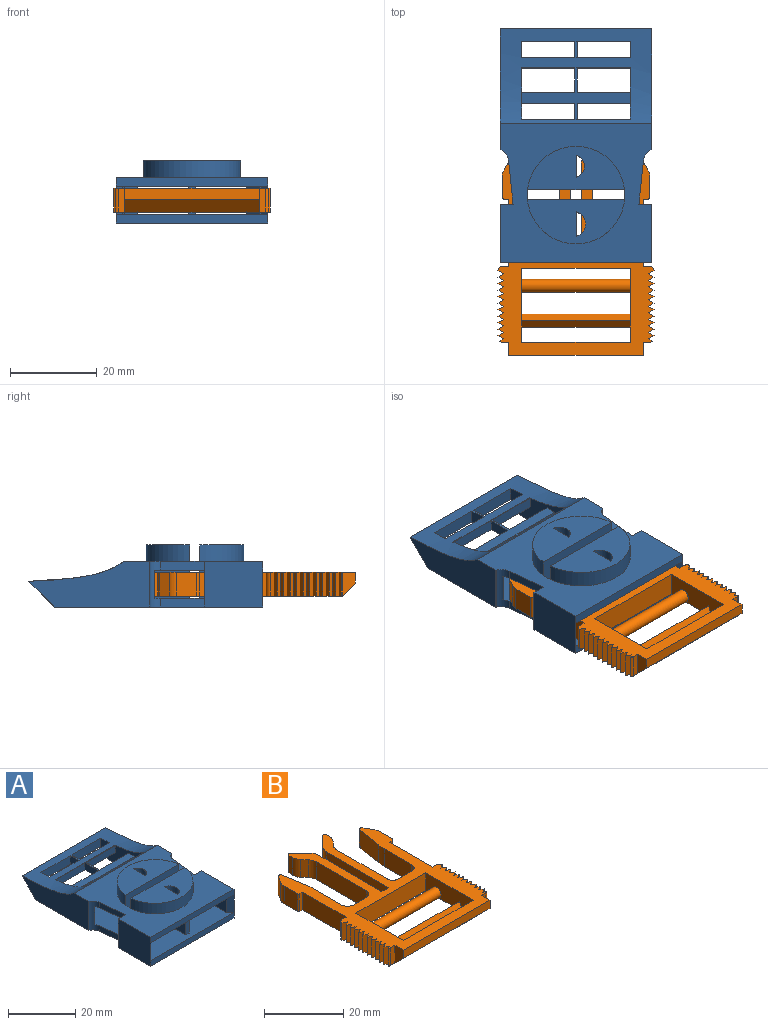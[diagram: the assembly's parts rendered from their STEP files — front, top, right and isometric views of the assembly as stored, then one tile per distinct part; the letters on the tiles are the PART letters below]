
ASSEMBLY  parts=2 mates=1
PART A: 76 faces, bbox 35x54x14.3 mm
  f0: cylinder r=11.25mm len=22.4mm, axis (0,0,-1), area 126.4mm2, adj f9,f29,f71
  f1: plane 48x35mm, normal (0,0,-1), area 1181.1mm2, adj f23,f24,f26,f27,f28,f32,f33,f34
  f2: plane 35x33mm, normal (0,0,1), area 912.1mm2, adj f4,f5,f6,f7,f23,f24,f25,f30
  f3: plane 35x33mm, normal (0,0,-1), area 912.1mm2, adj f4,f5,f6,f7,f23,f25,f30,f31
  f4: plane 16.2x6.5mm, normal (-1,0,0), area 105.3mm2, adj f2,f3,f23,f70
  f5: plane 8.53x6.5mm, normal (1,0,0), area 55.5mm2, adj f2,f3,f23,f69
  f6: plane 6.5x3.1mm, normal (1,0,0), area 20.2mm2, adj f2,f3,f67,f71
  f7: plane 6.5x3.15mm, normal (1,0,0), area 20.5mm2, adj f2,f3,f69,f70
  f8: plane 22.36x10.03mm, normal (0,0,1), area 163.8mm2, adj f65,f68,f69,f70
  f9: plane 22.4x10.22mm, normal (0,0,1), area 166.2mm2, adj f0,f66,f67,f71
  f10: plane 3.75x0.5mm, normal (0,0.06,1), area 1.9mm2, adj f12,f13,f44
  f11: plane 3.75x1mm, normal (0,-0.26,-0.97), area 1.9mm2, adj f12,f13,f17,f45
  f12: plane 3.75x3.3mm, normal (1,0,0), area 10.1mm2, adj f10,f11,f15,f35
  f13: plane 3.75x3.3mm, normal (-1,0,0), area 10.1mm2, adj f10,f11,f14,f36
  f14: plane 12.25x3.07mm, normal (0,-1,0), area 37.6mm2, adj f13,f33,f44,f45
  f15: plane 12.25x2.3mm, normal (0,1,0), area 28.1mm2, adj f12,f17,f32,f44
  f16: plane 25x11.93mm, normal (0,0,1), area 71.7mm2, adj f18,f19,f20,f21,f22,f23,f32,f33
  f17: plane 25x14.25mm, normal (0,0,-1), area 129.6mm2, adj f11,f15,f18,f19,f20,f21,f22,f23
  f18: plane 5.5x2.5mm, normal (1,0,0), area 13.7mm2, adj f16,f17,f20,f21
  f19: plane 5.5x2.5mm, normal (-1,0,0), area 13.7mm2, adj f16,f17,f41,f42
  f20: plane 12.25x2.5mm, normal (0,-1,0), area 30.6mm2, adj f16,f17,f18,f32
  f21: plane 12.25x2.5mm, normal (0,1,0), area 30.6mm2, adj f16,f17,f18,f32
  f22: plane 12.25x2.5mm, normal (0,-1,0), area 30.6mm2, adj f16,f17,f32,f63
  f23: plane 25x9.83mm, normal (0,1,0), area 91mm2, adj f1,f2,f3,f4,f5,f16,f17,f32
  f24: plane 35x2mm, normal (0,-1,0), area 70mm2, adj f1,f2,f27,f28
  f25: plane 6.5x0.4mm, normal (0,-1,0), area 2.6mm2, adj f2,f3,f38,f60
  f26: plane 27.93x10.5mm, normal (1,0,0), area 202mm2, adj f1,f29,f44,f45,f51
  f27: plane 13.5x10.5mm, normal (1,0,0), area 141.8mm2, adj f1,f24,f29,f37,f55,f61
  f28: plane 13.5x10.5mm, normal (-1,0,0), area 141.8mm2, adj f1,f24,f29,f37,f49,f62
  f29: plane 35x32.08mm, normal (0,0,1), area 668.9mm2, adj f0,f26,f27,f28,f34,f37,f44,f47
  f30: plane 12x6.5mm, normal (-1,0,0), area 78mm2, adj f2,f3,f55,f61
  f31: plane 6.5x3.15mm, normal (1,0,0), area 20.5mm2, adj f2,f3,f40,f48
  f32: plane 19.91x10.02mm, normal (-1,0,0), area 125.2mm2, adj f1,f2,f3,f15,f16,f17,f20,f21
  f33: plane 19.91x10.02mm, normal (1,0,0), area 125.2mm2, adj f1,f2,f3,f14,f16,f17,f23,f36
  f34: plane 27.93x10.5mm, normal (-1,0,0), area 202mm2, adj f1,f29,f44,f45,f50
  f35: plane 12.25x3.07mm, normal (0,-1,0), area 37.6mm2, adj f12,f32,f44,f45
  f36: plane 12.25x2.3mm, normal (0,1,0), area 28.1mm2, adj f13,f17,f33,f44
  f37: plane 35x2mm, normal (0,-1,0), area 70mm2, adj f3,f27,f28,f29
  f38: plane 6.5x3.15mm, normal (-1,0,0), area 20.5mm2, adj f2,f3,f25,f52
  f39: plane 12x6.5mm, normal (1,0,0), area 78mm2, adj f2,f3,f49,f62
  f40: plane 6.5x0.4mm, normal (0,-1,0), area 2.6mm2, adj f2,f3,f31,f59
  f41: plane 12.25x2.5mm, normal (0,-1,0), area 30.6mm2, adj f16,f17,f19,f33
  f42: plane 12.25x2.5mm, normal (0,1,0), area 30.6mm2, adj f16,f17,f19,f33
  f43: plane 12.25x2.5mm, normal (0,-1,0), area 30.6mm2, adj f16,f17,f33,f64
  f44: extruded ~35x21.85mm, area 386.4mm2, adj f10,f14,f15,f16,f23,f26,f29,f32
  f45: plane 35x5.92mm, normal (0,0.71,-0.71), area 187.2mm2, adj f1,f11,f14,f26,f32,f33,f34,f35
  f46: plane 10.07x2mm, normal (-0.99,-0.1,0), area 20.2mm2, adj f1,f2,f48,f49
  f47: plane 10.07x2mm, normal (-0.99,-0.1,0), area 20.2mm2, adj f3,f29,f48,f49
  f48: cylinder r=3mm len=10.5mm, axis (0,0,1), area 24.6mm2, adj f1,f2,f3,f29,f31,f46,f47,f50
  f49: plane 10.5x3mm, normal (0,1,0), area 21.8mm2, adj f1,f2,f3,f28,f29,f39,f46,f47
  f50: plane 10.5x0.14mm, normal (-0.39,-0.92,0), area 1.6mm2, adj f1,f29,f34,f48
  f51: plane 10.5x0.14mm, normal (0.39,-0.92,0), area 1.6mm2, adj f1,f26,f29,f52
  f52: cylinder r=3mm len=10.5mm, axis (0,0,1), area 24.6mm2, adj f1,f2,f3,f29,f38,f51,f53,f54
  f53: plane 10.07x2mm, normal (0.99,-0.1,0), area 20.2mm2, adj f1,f2,f52,f55
  f54: plane 10.07x2mm, normal (0.99,-0.1,0), area 20.2mm2, adj f3,f29,f52,f55
  f55: plane 10.5x3mm, normal (0,1,0), area 21.8mm2, adj f1,f2,f3,f27,f29,f30,f53,f54
  f56: plane 12.55x6.5mm, normal (-1,0,0), area 81.6mm2, adj f2,f3,f58,f71
  f57: plane 6.5x4.35mm, normal (1,0,0), area 28.3mm2, adj f2,f3,f58,f67
  f58: plane 6.5x1.4mm, normal (0,-1,0), area 9.1mm2, adj f2,f3,f56,f57
  f59: plane 6.5x3.1mm, normal (0.71,-0.71,0), area 28.5mm2, adj f2,f3,f33,f40
  f60: plane 6.5x3.1mm, normal (-0.71,-0.71,0), area 28.5mm2, adj f2,f3,f25,f32
  f61: plane 6.5x1.5mm, normal (-0.71,-0.71,0), area 13.8mm2, adj f2,f3,f27,f30
  f62: plane 6.5x1.5mm, normal (0.71,-0.71,0), area 13.8mm2, adj f2,f3,f28,f39
  f63: plane 3.75x2.5mm, normal (1,0,0), area 9.4mm2, adj f16,f17,f22,f23
  f64: plane 3.75x2.5mm, normal (-1,0,0), area 9.4mm2, adj f16,f17,f23,f43
  f65: cylinder r=11.25mm len=22.36mm, axis (0,0,-1), area 125mm2, adj f8,f29,f70
  f66: plane 14.3x5.61mm, normal (1,0,0), area 80.2mm2, adj f1,f9,f67
  f67: cylinder r=2.88mm len=14.3mm, axis (0,0,1), area 70.1mm2, adj f1,f2,f3,f6,f9,f57,f66
  f68: plane 14.3x5.1mm, normal (1,0,0), area 72.9mm2, adj f1,f8,f69
  f69: cylinder r=2.63mm len=14.3mm, axis (0,0,1), area 64.2mm2, adj f1,f2,f3,f5,f7,f8,f68
  f70: plane 22.36x14.3mm, normal (0,-1,0), area 183.5mm2, adj f1,f2,f3,f4,f7,f8,f65,f72
  f71: plane 22.4x14.3mm, normal (0,1,0), area 183.8mm2, adj f0,f1,f2,f3,f6,f9,f56,f72
  f72: cylinder r=11.25mm len=2.25mm, axis (0,0,1), area 4.5mm2, adj f1,f2,f70,f71
  f73: cylinder r=11.25mm len=2.25mm, axis (0,0,1), area 4.5mm2, adj f3,f29,f70,f71
  f74: cylinder r=11.25mm len=2.25mm, axis (0,0,1), area 4.5mm2, adj f1,f2,f70,f71
  f75: cylinder r=11.25mm len=2.25mm, axis (0,0,1), area 4.5mm2, adj f3,f29,f70,f71
PART B: 110 faces, bbox 36x50.4x5.5 mm
  f0: plane 5.5x3mm, normal (-1,0,0), area 12mm2, adj f2,f53,f57,f84
  f1: plane 5.5x3mm, normal (1,0,0), area 12mm2, adj f2,f53,f57,f58
  f2: plane 31x2.5mm, normal (0,-1,0), area 77.5mm2, adj f0,f1,f53,f57
  f3: plane 47.42x36mm, normal (0,0,-1), area 618.6mm2, adj f4,f6,f7,f8,f9,f10,f11,f12
  f4: plane 17x5.5mm, normal (-1,0,0), area 82.5mm2, adj f3,f5,f52,f53,f54,f55,f56
  f5: plane 25x5.5mm, normal (0,1,0), area 137.5mm2, adj f4,f6,f53,f57
  f6: plane 17x5.5mm, normal (1,0,0), area 82.5mm2, adj f3,f5,f52,f53,f54,f55,f56
  f7: plane 5.5x2.4mm, normal (0,1,0), area 13.2mm2, adj f3,f8,f51,f53
  f8: plane 22.52x5.5mm, normal (1,0,0), area 123.9mm2, adj f3,f7,f9,f53
  f9: cylinder r=3mm len=5.5mm, axis (0,0,-1), area 13mm2, adj f3,f8,f10,f53
  f10: plane 5.5x3.63mm, normal (0.71,0.71,0), area 28.2mm2, adj f3,f9,f11,f53
  f11: cylinder r=0.5mm len=5.5mm, axis (0,0,-1), area 6.5mm2, adj f3,f10,f12,f53
  f12: plane 5.5x1.43mm, normal (-1,0,0), area 7.8mm2, adj f3,f11,f13,f53
  f13: cylinder r=3mm len=5.5mm, axis (0,0,-1), area 12mm2, adj f3,f12,f14,f53
  f14: plane 5.5x1.49mm, normal (-0.75,-0.67,0), area 11mm2, adj f3,f13,f15,f53
  f15: cylinder r=3mm len=5.5mm, axis (0,0,-1), area 12mm2, adj f3,f14,f16,f53
  f16: plane 18x5.5mm, normal (-1,0,0), area 99mm2, adj f3,f15,f17,f53
  f17: cylinder r=2mm len=5.5mm, axis (0,0,-1), area 17.3mm2, adj f3,f16,f18,f53
  f18: plane 5.5x4.8mm, normal (0,1,0), area 26.4mm2, adj f3,f17,f19,f53
  f19: cylinder r=2mm len=5.5mm, axis (0,0,-1), area 17.3mm2, adj f3,f18,f20,f53
  f20: plane 9.84x5.5mm, normal (1,0,0), area 54.1mm2, adj f3,f19,f21,f53
  f21: cylinder r=15mm len=5.5mm, axis (0,0,-1), area 12.7mm2, adj f3,f20,f22,f53
  f22: plane 7.76x5.5mm, normal (0.99,0.15,0), area 43.2mm2, adj f3,f21,f23,f53
  f23: cylinder r=0.7mm len=5.5mm, axis (0,0,-1), area 9.5mm2, adj f3,f22,f24,f53
  f24: plane 5.5x2.45mm, normal (-0.87,0.5,0), area 15.6mm2, adj f3,f23,f25,f53
  f25: cylinder r=3mm len=5.5mm, axis (0,0,-1), area 8.6mm2, adj f3,f24,f26,f53
  f26: plane 5.5x4.7mm, normal (-1,0,0), area 25.8mm2, adj f3,f25,f27,f53
  f27: cylinder r=0.5mm len=5.5mm, axis (0,0,-1), area 4.3mm2, adj f3,f26,f28,f53
  f28: plane 5.5x1mm, normal (0,-1,0), area 5.5mm2, adj f3,f27,f29,f53
  f29: plane 15.5x5.5mm, normal (-1,0,0), area 85.2mm2, adj f3,f28,f53,f87
  f30: plane 15.5x5.5mm, normal (1,0,0), area 85.2mm2, adj f3,f31,f53,f61
  f31: plane 5.5x1mm, normal (0,-1,0), area 5.5mm2, adj f3,f30,f32,f53
  f32: cylinder r=0.5mm len=5.5mm, axis (0,0,-1), area 4.3mm2, adj f3,f31,f33,f53
  f33: plane 5.5x4.7mm, normal (1,0,0), area 25.8mm2, adj f3,f32,f34,f53
  f34: cylinder r=3mm len=5.5mm, axis (0,0,-1), area 8.6mm2, adj f3,f33,f35,f53
  f35: plane 5.5x2.45mm, normal (0.87,0.5,0), area 15.6mm2, adj f3,f34,f36,f53
  f36: cylinder r=0.7mm len=5.5mm, axis (0,0,-1), area 9.5mm2, adj f3,f35,f37,f53
  f37: plane 7.76x5.5mm, normal (-0.99,0.15,0), area 43.2mm2, adj f3,f36,f38,f53
  f38: cylinder r=15mm len=5.5mm, axis (0,0,-1), area 12.7mm2, adj f3,f37,f39,f53
  f39: plane 9.84x5.5mm, normal (-1,0,0), area 54.1mm2, adj f3,f38,f40,f53
  f40: cylinder r=2mm len=5.5mm, axis (0,0,-1), area 17.3mm2, adj f3,f39,f41,f53
  f41: plane 5.5x4.8mm, normal (0,1,0), area 26.4mm2, adj f3,f40,f42,f53
  f42: cylinder r=2mm len=5.5mm, axis (0,0,-1), area 17.3mm2, adj f3,f41,f43,f53
  f43: plane 18x5.5mm, normal (1,0,0), area 99mm2, adj f3,f42,f44,f53
  f44: cylinder r=3mm len=5.5mm, axis (0,0,-1), area 12mm2, adj f3,f43,f45,f53
  f45: plane 5.5x1.49mm, normal (0.75,-0.67,0), area 11mm2, adj f3,f44,f46,f53
  f46: cylinder r=3mm len=5.5mm, axis (0,0,-1), area 12mm2, adj f3,f45,f47,f53
  f47: plane 5.5x1.16mm, normal (1,0,0), area 6.4mm2, adj f3,f46,f48,f53
  f48: cylinder r=0.5mm len=5.5mm, axis (0,0,-1), area 6.5mm2, adj f3,f47,f49,f53
  f49: plane 5.5x3.63mm, normal (-0.71,0.71,0), area 28.2mm2, adj f3,f48,f50,f53
  f50: cylinder r=3mm len=5.5mm, axis (0,0,-1), area 13mm2, adj f3,f49,f51,f53
  f51: plane 22.26x5.5mm, normal (-1,0,0), area 122.4mm2, adj f3,f7,f50,f53
  f52: plane 25x5.5mm, normal (0,-1,0), area 137.5mm2, adj f3,f4,f6,f53
  f53: plane 50.42x36mm, normal (0,0,1), area 636.6mm2, adj f0,f1,f2,f4,f5,f6,f7,f8
  f54: plane 25x2.6mm, normal (0,0.87,0.5), area 75mm2, adj f3,f4,f6,f55
  f55: plane 25x2.6mm, normal (0,-0.87,0.5), area 75mm2, adj f3,f4,f6,f54
  f56: cylinder r=1.5mm len=25mm, axis (-1,0,0), area 235.6mm2, adj f4,f6
  f57: plane 31x3mm, normal (0,-0.71,-0.71), area 131.5mm2, adj f0,f1,f2,f3,f5
  f58: plane 5.5x1.5mm, normal (0,-1,0), area 8.2mm2, adj f1,f3,f53,f59
  f59: cylinder r=1mm len=5.5mm, axis (0,0,1), area 3.7mm2, adj f3,f53,f58,f81
  f60: cylinder r=1mm len=5.5mm, axis (0,0,1), area 8.6mm2, adj f3,f53,f61,f82
  f61: plane 5.5x1.5mm, normal (0,1,0), area 8.2mm2, adj f3,f30,f53,f60
  f62: plane 5.5x1.3mm, normal (0.5,-0.87,0), area 8.2mm2, adj f3,f53,f63,f79
  f63: plane 5.5x1.3mm, normal (0.5,0.87,0), area 8.2mm2, adj f3,f53,f62,f80
  f64: plane 5.5x1.3mm, normal (0.5,-0.87,0), area 8.2mm2, adj f3,f53,f65,f77
  f65: plane 5.5x1.3mm, normal (0.5,0.87,0), area 8.2mm2, adj f3,f53,f64,f78
  f66: plane 5.5x1.3mm, normal (0.5,-0.87,0), area 8.2mm2, adj f3,f53,f67,f75
  f67: plane 5.5x1.3mm, normal (0.5,0.87,0), area 8.2mm2, adj f3,f53,f66,f76
  f68: plane 5.5x1.3mm, normal (0.5,-0.87,0), area 8.2mm2, adj f3,f53,f69,f73
  f69: plane 5.5x1.3mm, normal (0.5,0.87,0), area 8.2mm2, adj f3,f53,f68,f74
  f70: plane 5.5x1.3mm, normal (0.5,-0.87,0), area 8.2mm2, adj f3,f53,f71,f83
  f71: plane 5.5x1.3mm, normal (0.5,0.87,0), area 8.2mm2, adj f3,f53,f70,f72
  f72: plane 5.5x1.3mm, normal (0.5,-0.87,0), area 8.2mm2, adj f3,f53,f71,f73
  f73: plane 5.5x1.3mm, normal (0.5,0.87,0), area 8.2mm2, adj f3,f53,f68,f72
  f74: plane 5.5x1.3mm, normal (0.5,-0.87,0), area 8.2mm2, adj f3,f53,f69,f75
  f75: plane 5.5x1.3mm, normal (0.5,0.87,0), area 8.2mm2, adj f3,f53,f66,f74
  f76: plane 5.5x1.3mm, normal (0.5,-0.87,0), area 8.2mm2, adj f3,f53,f67,f77
  f77: plane 5.5x1.3mm, normal (0.5,0.87,0), area 8.2mm2, adj f3,f53,f64,f76
  f78: plane 5.5x1.3mm, normal (0.5,-0.87,0), area 8.2mm2, adj f3,f53,f65,f79
  f79: plane 5.5x1.3mm, normal (0.5,0.87,0), area 8.2mm2, adj f3,f53,f62,f78
  f80: plane 5.5x1.3mm, normal (0.5,-0.87,0), area 8.2mm2, adj f3,f53,f63,f81
  f81: plane 5.5x0.92mm, normal (0.5,0.87,0), area 5.9mm2, adj f3,f53,f59,f80
  f82: plane 5.5x1.3mm, normal (0.5,-0.87,0), area 8.2mm2, adj f3,f53,f60,f83
  f83: plane 5.5x1.3mm, normal (0.5,0.87,0), area 8.2mm2, adj f3,f53,f70,f82
  f84: plane 5.5x1.5mm, normal (0,-1,0), area 8.2mm2, adj f0,f3,f53,f85
  f85: cylinder r=1mm len=5.5mm, axis (0,0,1), area 3.7mm2, adj f3,f53,f84,f107
  f86: cylinder r=1mm len=5.5mm, axis (0,0,1), area 8.6mm2, adj f3,f53,f87,f108
  f87: plane 5.5x1.5mm, normal (0,1,0), area 8.2mm2, adj f3,f29,f53,f86
  f88: plane 5.5x1.3mm, normal (-0.5,-0.87,0), area 8.2mm2, adj f3,f53,f89,f105
  f89: plane 5.5x1.3mm, normal (-0.5,0.87,0), area 8.2mm2, adj f3,f53,f88,f106
  f90: plane 5.5x1.3mm, normal (-0.5,-0.87,0), area 8.2mm2, adj f3,f53,f91,f103
  f91: plane 5.5x1.3mm, normal (-0.5,0.87,0), area 8.2mm2, adj f3,f53,f90,f104
  f92: plane 5.5x1.3mm, normal (-0.5,-0.87,0), area 8.2mm2, adj f3,f53,f93,f101
  f93: plane 5.5x1.3mm, normal (-0.5,0.87,0), area 8.2mm2, adj f3,f53,f92,f102
  f94: plane 5.5x1.3mm, normal (-0.5,-0.87,0), area 8.2mm2, adj f3,f53,f95,f99
  f95: plane 5.5x1.3mm, normal (-0.5,0.87,0), area 8.2mm2, adj f3,f53,f94,f100
  f96: plane 5.5x1.3mm, normal (-0.5,-0.87,0), area 8.2mm2, adj f3,f53,f97,f109
  f97: plane 5.5x1.3mm, normal (-0.5,0.87,0), area 8.2mm2, adj f3,f53,f96,f98
  f98: plane 5.5x1.3mm, normal (-0.5,-0.87,0), area 8.2mm2, adj f3,f53,f97,f99
  f99: plane 5.5x1.3mm, normal (-0.5,0.87,0), area 8.2mm2, adj f3,f53,f94,f98
  f100: plane 5.5x1.3mm, normal (-0.5,-0.87,0), area 8.2mm2, adj f3,f53,f95,f101
  f101: plane 5.5x1.3mm, normal (-0.5,0.87,0), area 8.2mm2, adj f3,f53,f92,f100
  f102: plane 5.5x1.3mm, normal (-0.5,-0.87,0), area 8.2mm2, adj f3,f53,f93,f103
  f103: plane 5.5x1.3mm, normal (-0.5,0.87,0), area 8.2mm2, adj f3,f53,f90,f102
  f104: plane 5.5x1.3mm, normal (-0.5,-0.87,0), area 8.2mm2, adj f3,f53,f91,f105
  f105: plane 5.5x1.3mm, normal (-0.5,0.87,0), area 8.2mm2, adj f3,f53,f88,f104
  f106: plane 5.5x1.3mm, normal (-0.5,-0.87,0), area 8.2mm2, adj f3,f53,f89,f107
  f107: plane 5.5x0.92mm, normal (-0.5,0.87,0), area 5.9mm2, adj f3,f53,f85,f106
  f108: plane 5.5x1.3mm, normal (-0.5,-0.87,0), area 8.2mm2, adj f3,f53,f86,f109
  f109: plane 5.5x1.3mm, normal (-0.5,0.87,0), area 8.2mm2, adj f3,f53,f96,f108
PLACE A at identity fixed
PLACE B t=(0,-23.97,2.5)mm
MATE slider A.f58 <-> B.f7  axis (0,-1,0) through (0,-25,5.25)mm
